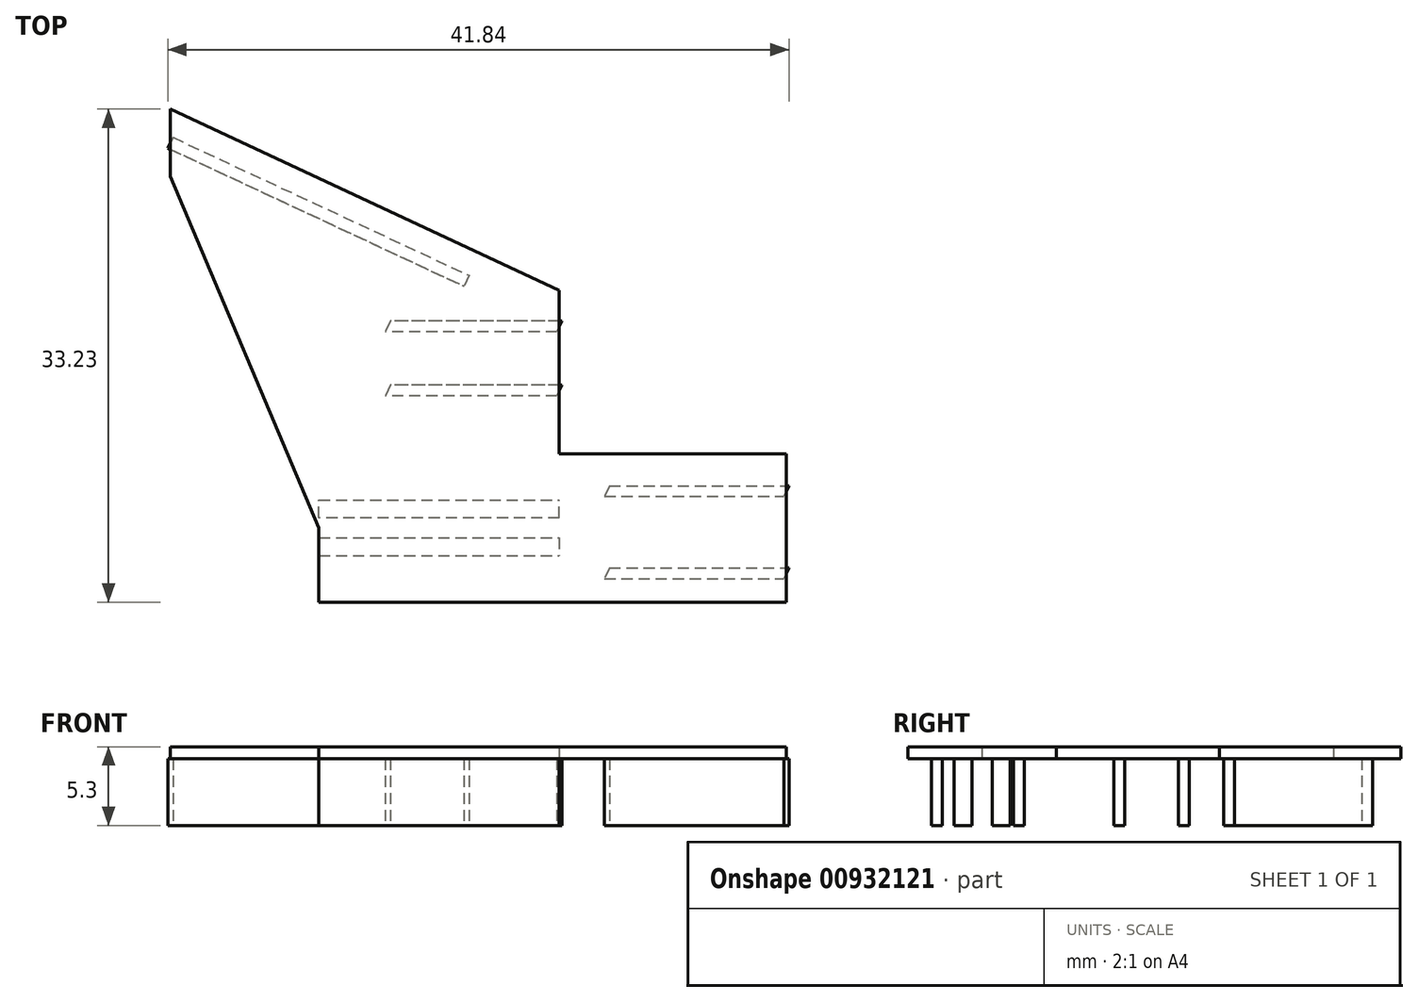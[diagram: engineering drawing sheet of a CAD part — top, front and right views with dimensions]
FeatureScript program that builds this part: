
annotation { "Feature Type Name" : "Feature", "Feature Type Description" : "" }
export const myFeature = defineFeature(function(context is Context, id is Id, definition is map)
    precondition{}
    {
        {
            var Q0;
            Q0=qCreatedBy(makeId("Top.planeOp"),FACE);
            var sketch = newSketch(context, id + "F0", { "sketchPlane" : qUnion([Q0])});
            skLineSegment(sketch, "E0", {"start": v(-37.86, 16.82) * mm, "end": v(-21.66, 16.82) * mm});
            skLineSegment(sketch, "E1", {"start": v(-21.66, 16.82) * mm, "end": v(-21.66, 18.17) * mm});
            skLineSegment(sketch, "E2", {"start": v(-21.66, 18.17) * mm, "end": v(-37.86, 18.17) * mm});
            skLineSegment(sketch, "E3", {"start": v(-37.86, 18.17) * mm, "end": v(-37.86, 16.82) * mm});
            skLineSegment(sketch, "E4", {"start": v(-37.86, 18.17) * mm, "end": v(-37.86, 19.37) * mm});
            skLineSegment(sketch, "E5", {"start": v(-37.86, 19.37) * mm, "end": v(-21.66, 19.37) * mm});
            skLineSegment(sketch, "E6", {"start": v(-21.66, 18.17) * mm, "end": v(-21.66, 19.37) * mm});
            skLineSegment(sketch, "E7", {"start": v(-37.86, 17.5) * mm, "end": v(-21.66, 17.5) * mm, "construction": true});
            skLineSegment(sketch, "E8.MirrorCS", {"start": v(-37.86, 15.62) * mm, "end": v(-21.66, 15.62) * mm});
            skLineSegment(sketch, "E9.MirrorCS", {"start": v(-21.66, 16.82) * mm, "end": v(-21.66, 15.62) * mm});
            skLineSegment(sketch, "E10.MirrorCS", {"start": v(-37.86, 16.82) * mm, "end": v(-37.86, 15.62) * mm});
            skSolve(sketch);
        }
        {
            var Q0;
            Q0=makeQuery(id+"F0.imprint","IMPRINT",FACE,{"disambiguationData":[TD([[makeQuery(id+"F0.imprint","IMPRINT",EDGE,{"derivedFrom":sQuery(id+"F0.wireOp",EDGE,"E2")}),-1.0]])]});
            var Q1;
            Q1=makeQuery(id+"F0.imprint","IMPRINT",FACE,{"disambiguationData":[TD([[makeQuery(id+"F0.imprint","IMPRINT",EDGE,{"derivedFrom":sQuery(id+"F0.wireOp",EDGE,"E0")}),-1.0]])]});
            extrude(context, id + "F1", {"entities" : qUnion([Q0, Q1]), "depth" : 4.5 * mm, "offsetDistance" : 25 * mm});
        }
        {
            var Q0;
            Q0=makeQuery(id+"F1.opExtrude","CAP_FACE",FACE,{"disambiguationData":[OSD([sQuery(id+"F0.wireOp",EDGE,"E0"),sQuery(id+"F0.wireOp",EDGE,"E8.MirrorCS"),sQuery(id+"F0.wireOp",EDGE,"E9.MirrorCS"),sQuery(id+"F0.wireOp",EDGE,"E10.MirrorCS")])],"isStart":false});
            var sketch = newSketch(context, id + "F2", { "sketchPlane" : qUnion([Q0])});
            skLineSegment(sketch, "E11.0", {"start": v(-37.86, 17.5) * mm, "end": v(-21.66, 17.5) * mm});
            skLineSegment(sketch, "E12", {"start": v(-21.66, 17.5) * mm, "end": v(-21.66, 12.5) * mm});
            skLineSegment(sketch, "E13", {"start": v(-21.66, 17.5) * mm, "end": v(-21.66, 33.5) * mm});
            skLineSegment(sketch, "E14", {"start": v(-37.86, 17.5) * mm, "end": v(-47.86, 41.18) * mm});
            skLineSegment(sketch, "E15", {"start": v(-37.86, 17.5) * mm, "end": v(-47.86, 17.5) * mm, "construction": true});
            skLineSegment(sketch, "E16", {"start": v(-47.86, 17.5) * mm, "end": v(-47.86, 50.8) * mm, "construction": true});
            skLineSegment(sketch, "E17", {"start": v(-37.86, 17.5) * mm, "end": v(-53.86, 17.5) * mm, "construction": true});
            skLineSegment(sketch, "E18", {"start": v(-47.86, 41.18) * mm, "end": v(-47.86, 45.72) * mm});
            skLineSegment(sketch, "E19", {"start": v(-47.86, 45.72) * mm, "end": v(-21.66, 33.5) * mm});
            skLineSegment(sketch, "E20", {"start": v(-21.66, 12.5) * mm, "end": v(-6.36, 12.5) * mm});
            skLineSegment(sketch, "E21.MirrorCS", {"start": v(-21.66, 17.5) * mm, "end": v(-21.66, 22.5) * mm});
            skLineSegment(sketch, "E22.MirrorCS", {"start": v(-21.66, 22.5) * mm, "end": v(-6.36, 22.5) * mm});
            skLineSegment(sketch, "E23", {"start": v(-6.36, 22.5) * mm, "end": v(-6.36, 12.5) * mm});
            skLineSegment(sketch, "E24", {"start": v(-21.66, 12.5) * mm, "end": v(-37.86, 12.5) * mm});
            skLineSegment(sketch, "E25", {"start": v(-37.86, 12.5) * mm, "end": v(-37.86, 17.5) * mm});
            skSolve(sketch);
        }
        {
            var Q0;
            Q0=makeQuery(id+"F2.imprint","IMPRINT",FACE,{"disambiguationData":[TD([[makeQuery(id+"F2.imprint","IMPRINT",EDGE,{"derivedFrom":sQuery(id+"F2.wireOp",EDGE,"E11.0")}),1.0]])]});
            var Q1;
            {var subQ0=sQuery(id+"F2.wireOp",EDGE,"E20");Q1=makeQuery(id+"F2.imprint","IMPRINT",FACE,{"disambiguationData":[TD([[makeQuery(id+"F2.imprint","IMPRINT",EDGE,{"derivedFrom":subQ0}),1.0]])]});}
            var Q2;
            {var subQ4=sQuery(id+"F2.wireOp",EDGE,"E12");Q2=makeQuery(id+"F2.imprint","IMPRINT",FACE,{"disambiguationData":[TD([[makeQuery(id+"F2.imprint","IMPRINT",EDGE,{"derivedFrom":subQ4}),-1.0]])]});}
            var Q3;
            {var subQ0=sQuery(id+"F2.wireOp",EDGE,"E11.0");Q3=makeQuery(id+"F2.imprint","IMPRINT",FACE,{"disambiguationData":[TD([[makeQuery(id+"F2.imprint","IMPRINT",EDGE,{"derivedFrom":subQ0}),-1.0]])]});}
            var Q4;
            {var subQ1=makeQuery(id+"F1.opExtrude","CAP_EDGE",EDGE,{"disambiguationData":[OSD([sQuery(id+"F0.wireOp",EDGE,"E0")])],"isStart":false});Q4=makeQuery(id+"F2.imprint","IMPRINT",FACE,{"disambiguationData":[TD([[makeQuery(id+"F2.imprint","IMPRINT",EDGE,{"derivedFrom":subQ1}),-1.0]])]});}
            var Q5;
            {var subQ2=sQuery(id+"F2.wireOp",EDGE,"E24");Q5=makeQuery(id+"F2.imprint","IMPRINT",FACE,{"disambiguationData":[TD([[makeQuery(id+"F2.imprint","IMPRINT",EDGE,{"derivedFrom":subQ2}),-1.0]])]});}
            extrude(context, id + "F3", {"entities" : qUnion([Q0, Q1, Q2, Q3, Q4, Q5]), "operationType" : NewBodyOperationType.ADD, "depth" : .8 * mm, "offsetDistance" : 25 * mm});
        }
        {
            var Q0;
            Q0=makeQuery(id+"F2.imprint","IMPRINT",FACE,{"disambiguationData":[TD([[makeQuery(id+"F2.imprint","IMPRINT",EDGE,{"derivedFrom":sQuery(id+"F2.wireOp",EDGE,"E11.0")}),1.0]])]});
            var sketch = newSketch(context, id + "F4", { "sketchPlane" : qUnion([Q0])});
            skLineSegment(sketch, "E26.0", {"start": v(-47.86, 45.72) * mm, "end": v(-21.66, 33.5) * mm});
            skLineSegment(sketch, "E27.0.0", {"start": v(-21.66, 16.82) * mm, "end": v(-37.86, 16.82) * mm});
            skLineSegment(sketch, "E27.0.1", {"start": v(-37.86, 16.82) * mm, "end": v(-37.86, 17.5) * mm});
            skLineSegment(sketch, "E27.0.2", {"start": v(-37.86, 17.5) * mm, "end": v(-47.86, 41.18) * mm});
            skLineSegment(sketch, "E27.0.3", {"start": v(-47.86, 41.18) * mm, "end": v(-47.86, 45.72) * mm});
            skLineSegment(sketch, "E27.0.5", {"start": v(-21.66, 33.5) * mm, "end": v(-21.66, 22.5) * mm});
            skLineSegment(sketch, "E27.0.6", {"start": v(-21.66, 22.5) * mm, "end": v(-6.36, 22.5) * mm});
            skLineSegment(sketch, "E27.0.7", {"start": v(-6.36, 22.5) * mm, "end": v(-6.36, 12.5) * mm});
            skLineSegment(sketch, "E27.0.8", {"start": v(-6.36, 12.5) * mm, "end": v(-6.36, 12.5) * mm});
            skLineSegment(sketch, "E27.0.12", {"start": v(-37.86, 15.62) * mm, "end": v(-21.66, 15.62) * mm});
            skLineSegment(sketch, "E27.0.13", {"start": v(-21.66, 15.62) * mm, "end": v(-21.66, 16.82) * mm});
            skLineSegment(sketch, "E28", {"start": v(-47.86, 43.45) * mm, "end": v(-27.92, 34.14) * mm});
            skLineSegment(sketch, "E29", {"start": v(-18.46, 19.98) * mm, "end": v(-6.36, 19.98) * mm});
            skLineSegment(sketch, "E30", {"start": v(-18.46, 14.45) * mm, "end": v(-6.36, 14.45) * mm});
            skLineSegment(sketch, "E31", {"start": v(-21.66, 31.07) * mm, "end": v(-33.23, 31.07) * mm});
            skLineSegment(sketch, "E32", {"start": v(-21.66, 26.75) * mm, "end": v(-33.23, 26.75) * mm});
            skSolve(sketch);
        }
        {
            var Q0;
            Q0=sQuery(id+"F4.wireOp",EDGE,"E28");
            var Q1;
            Q1=sQuery(id+"F4.wireOp",EDGE,"E29");
            var Q2;
            Q2=sQuery(id+"F4.wireOp",EDGE,"E30");
            var Q3;
            Q3=sQuery(id+"F4.wireOp",EDGE,"E31");
            var Q4;
            Q4=sQuery(id+"F4.wireOp",EDGE,"E32");
            extrude(context, id + "F5", {"bodyType" : ToolBodyType.SURFACE, "surfaceEntities" : qUnion([Q0, Q1, Q2, Q3, Q4]), "oppositeDirection" : true, "depth" : 4.5 * mm, "offsetDistance" : 25 * mm});
        }
        {
            var Q0;
            Q0=makeQuery(id+"F5.opExtrude","SWEPT_FACE",FACE,{"disambiguationData":[OSD([sQuery(id+"F4.wireOp",EDGE,"E28")])]});
            var Q1;
            Q1=makeQuery(id+"F5.opExtrude","SWEPT_FACE",FACE,{"disambiguationData":[OSD([sQuery(id+"F4.wireOp",EDGE,"E29")])]});
            var Q2;
            Q2=makeQuery(id+"F5.opExtrude","SWEPT_FACE",FACE,{"disambiguationData":[OSD([sQuery(id+"F4.wireOp",EDGE,"E30")])]});
            var Q3;
            Q3=makeQuery(id+"F5.opExtrude","SWEPT_FACE",FACE,{"disambiguationData":[OSD([sQuery(id+"F4.wireOp",EDGE,"E31")])]});
            var Q4;
            Q4=makeQuery(id+"F5.opExtrude","SWEPT_FACE",FACE,{"disambiguationData":[OSD([sQuery(id+"F4.wireOp",EDGE,"E32")])]});
            extrude(context, id + "F6", {"entities" : qUnion([Q0, Q1, Q2, Q3, Q4]), "operationType" : NewBodyOperationType.ADD, "endBound" : BoundingType.SYMMETRIC, "depth" : .8 * mm, "offsetDistance" : 25 * mm});
        }
    });
